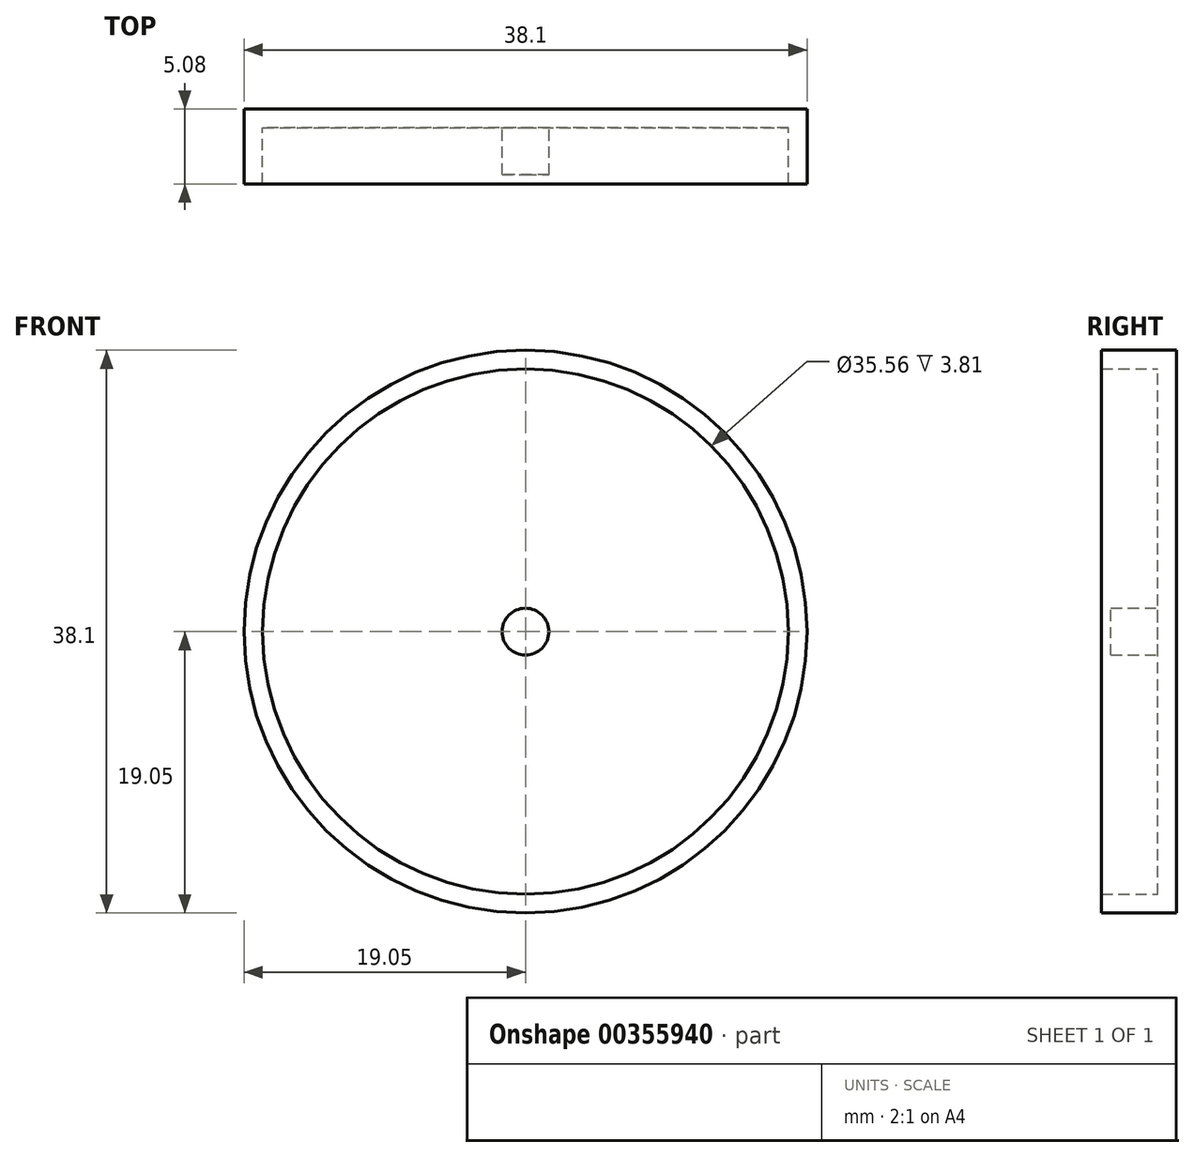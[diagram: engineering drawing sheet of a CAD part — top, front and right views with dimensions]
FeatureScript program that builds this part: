
annotation { "Feature Type Name" : "Feature", "Feature Type Description" : "" }
export const myFeature = defineFeature(function(context is Context, id is Id, definition is map)
    precondition{}
    {
        {
            var Q0;
            Q0=qCreatedBy(makeId("Front.planeOp"),FACE);
            var sketch = newSketch(context, id + "F0", { "sketchPlane" : qUnion([Q0])});
            skCircle(sketch, "E0", {"center": v(0, 0) * mm, "radius": 19.05 * mm});
            skSolve(sketch);
        }
        {
            var Q0;
            Q0=qSketchRegion(id+"F0",true);
            extrude(context, id + "F1", {"entities" : qUnion([Q0]), "depth" : 5.08 * mm});
        }
        {
            var Q0;
            Q0=makeQuery(id+"F1.opExtrude","CAP_FACE",FACE,{"disambiguationData":[OSD([sQuery(id+"F0.wireOp",EDGE,"E0")])],"isStart":false});
            shell(context, id + "F2", {"entities" : qUnion([Q0]), "thickness" : 1.27 * mm});
        }
        {
            var Q0;
            {var subQ0=sQuery(id+"F0.wireOp",EDGE,"E0");Q0=makeQuery(id+"F2.opShell","OFFSET_FACE",FACE,{"disambiguationData":[OSD([subQ0]),TDD([makeQuery(id+"F1.opExtrude","CAP_FACE",FACE,{"disambiguationData":[OSD([subQ0])],"isStart":true})])]});}
            var sketch = newSketch(context, id + "F3", { "sketchPlane" : qUnion([Q0])});
            skCircle(sketch, "E1", {"center": v(0, 0) * mm, "radius": 1.59 * mm});
            skSolve(sketch);
        }
        {
            var Q0;
            Q0=makeQuery(id+"F3.imprint","IMPRINT",FACE,{"disambiguationData":[TD([[makeQuery(id+"F3.imprint","IMPRINT",EDGE,{"derivedFrom":sQuery(id+"F3.wireOp",EDGE,"E1")}),1.0]])]});
            extrude(context, id + "F4", {"entities" : qUnion([Q0]), "operationType" : NewBodyOperationType.ADD, "depth" : 3.17 * mm});
        }
    });
